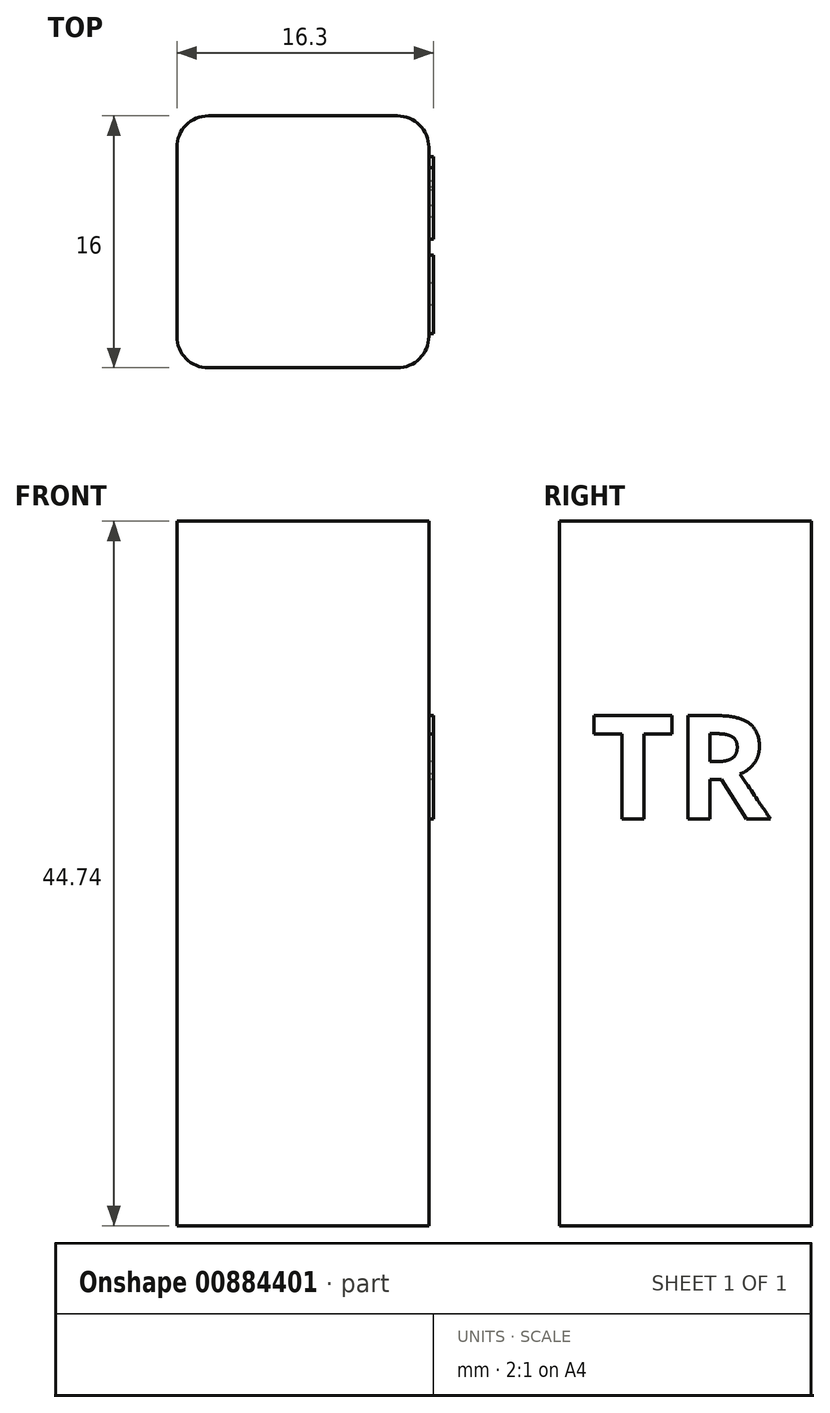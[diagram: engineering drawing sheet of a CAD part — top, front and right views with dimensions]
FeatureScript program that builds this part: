
annotation { "Feature Type Name" : "Feature", "Feature Type Description" : "" }
export const myFeature = defineFeature(function(context is Context, id is Id, definition is map)
    precondition{}
    {
        {
            var Q0;
            Q0=qCreatedBy(makeId("Top.planeOp"),FACE);
            var sketch = newSketch(context, id + "F0", { "sketchPlane" : qUnion([Q0])});
            skLineSegment(sketch, "E0.bottom", {"start": v(0, 0) * mm, "end": v(16, 0) * mm});
            skLineSegment(sketch, "E0.top", {"start": v(0, 16) * mm, "end": v(16, 16) * mm});
            skLineSegment(sketch, "E0.left", {"start": v(0, 0) * mm, "end": v(0, 16) * mm});
            skLineSegment(sketch, "E0.right", {"start": v(16, 0) * mm, "end": v(16, 16) * mm});
            skSolve(sketch);
        }
        {
            var Q0;
            Q0=qSketchRegion(id+"F0",true);
            extrude(context, id + "F1", {"entities" : qUnion([Q0]), "depth" : 44.74 * mm, "offsetDistance" : 25 * mm});
        }
        {
            var Q0;
            Q0=makeQuery(id+"F1.opExtrude","SWEPT_EDGE",EDGE,{"disambiguationData":[OSD([sQuery(id+"F0.wireOp",EDGE,"E0.bottom"),sQuery(id+"F0.wireOp",EDGE,"E0.right")])]});
            var Q1;
            Q1=makeQuery(id+"F1.opExtrude","SWEPT_EDGE",EDGE,{"disambiguationData":[OSD([sQuery(id+"F0.wireOp",EDGE,"E0.bottom"),sQuery(id+"F0.wireOp",EDGE,"E0.left")])]});
            var Q2;
            Q2=makeQuery(id+"F1.opExtrude","SWEPT_EDGE",EDGE,{"disambiguationData":[OSD([sQuery(id+"F0.wireOp",EDGE,"E0.top"),sQuery(id+"F0.wireOp",EDGE,"E0.right")])]});
            var Q3;
            Q3=makeQuery(id+"F1.opExtrude","SWEPT_EDGE",EDGE,{"disambiguationData":[OSD([sQuery(id+"F0.wireOp",EDGE,"E0.top"),sQuery(id+"F0.wireOp",EDGE,"E0.left")])]});
            fillet(context, id + "F2", {"entities" : qUnion([Q0, Q1, Q2, Q3]), "radius" : 2 * mm, "tangentPropagation" : true, "allowEdgeOverflow" : false});
        }
        {
            var Q0;
            Q0=makeQuery(id+"F1.opExtrude","SWEPT_FACE",FACE,{"disambiguationData":[OSD([sQuery(id+"F0.wireOp",EDGE,"E0.right")])]});
            var sketch = newSketch(context, id + "F3", { "sketchPlane" : qUnion([Q0])});
            skText(sketch, "E1", { "text": "TR", "fontName": "OpenSans-Bold.ttf"});
            const initialGuessF3  = {"E1": [0.002, 0.02582, 1, 0, 0.00663]};
            skSetInitialGuess(sketch, initialGuessF3);
            skSolve(sketch);
        }
        {
            var Q0;
            Q0=qSketchRegion(id+"F3",true);
            extrude(context, id + "F4", {"entities" : qUnion([Q0]), "operationType" : NewBodyOperationType.ADD, "depth" : 0.3 * mm, "offsetDistance" : 25 * mm});
        }
    });
